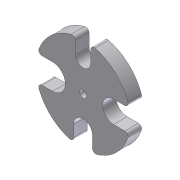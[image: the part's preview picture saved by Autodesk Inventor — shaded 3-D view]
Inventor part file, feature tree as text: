
AUTODESK INVENTOR PART (.ipt)
format: ipt  version: unknown  size: 219,136 bytes
history: native  units: mm (DEFAULTED — no unit token found)
features: extrude x3, sketch x3, fillet x1
ambient origin geometry x8: Origin, YZ Plane, XZ Plane, XY Plane, X Axis, Y Axis, Z Axis, Center Point
feature tree (7):
  extrude  "Extrusion1"  Depth=12.7mm TaperAngle=0.0deg
  extrude  "Extrusion2"  Depth=28.575mm
  fillet  "Fillet1"  Radius=12.7mm
  extrude  "Extrusion3"  Depth=28.575mm
  sketch  "Sketch1"  dims[d0=88.9mm d1=12.7mm d2=0.0mm]
  sketch  "Sketch2"  dims[d3=14.2748mm d4=28.575mm d5=12.7mm d6=0.0mm]
  sketch  "Sketch3"  dims[d7=8.7249mm d8=28.575mm d9=23.7998mm d10=20.6248mm d11=3.175mm d12=6.35mm d13=12.7mm d14=0.0mm]
